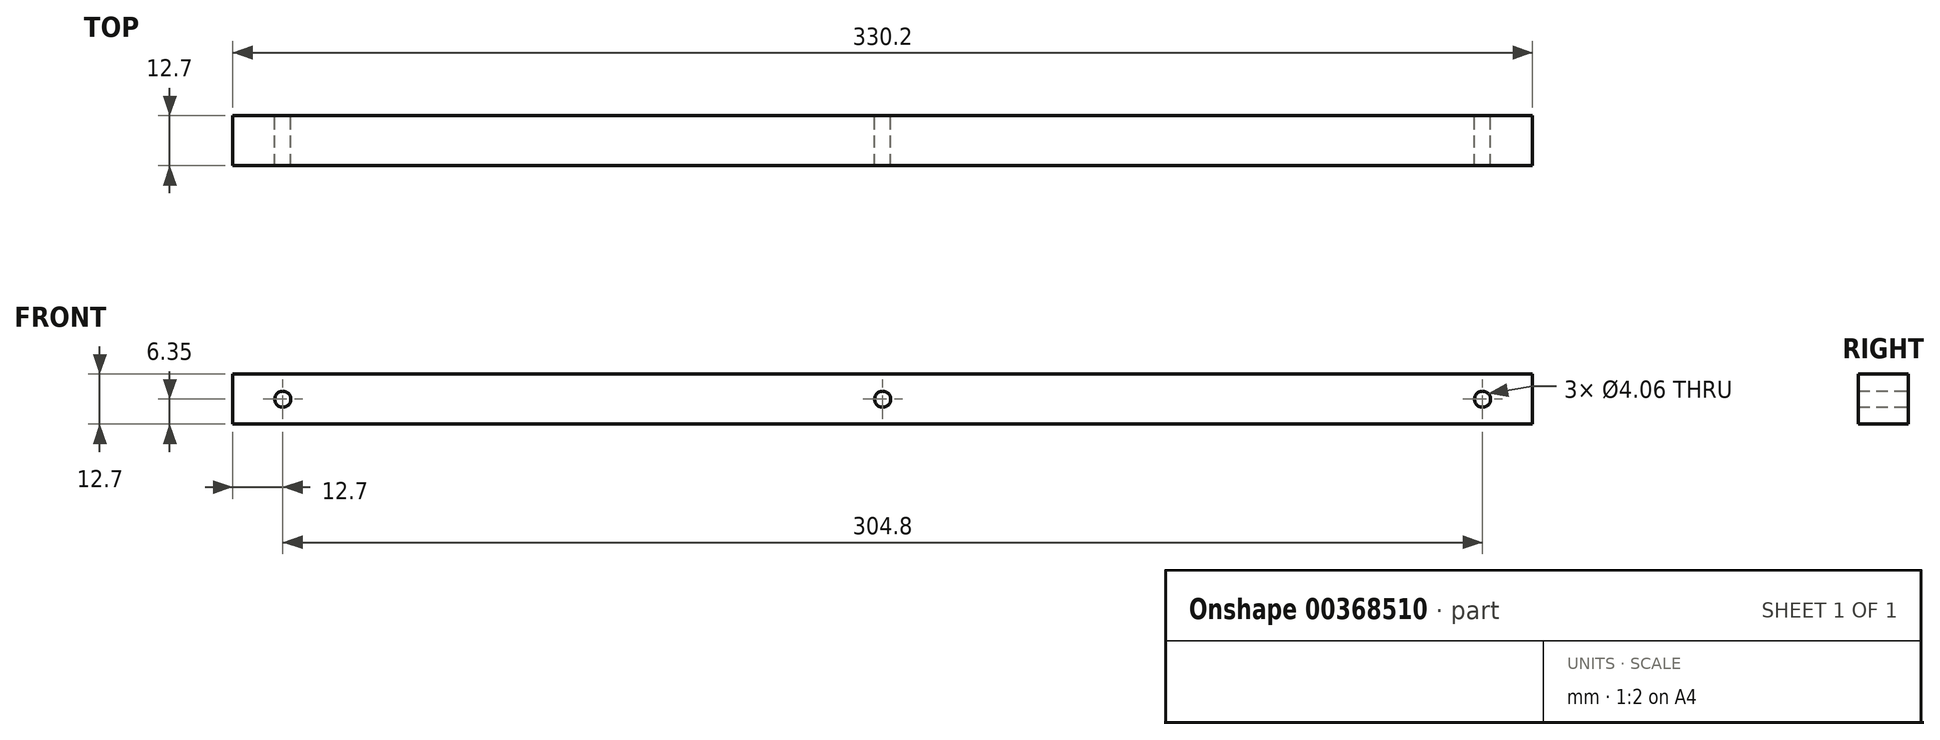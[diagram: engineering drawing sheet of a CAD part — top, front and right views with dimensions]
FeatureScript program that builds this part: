
annotation { "Feature Type Name" : "Feature", "Feature Type Description" : "" }
export const myFeature = defineFeature(function(context is Context, id is Id, definition is map)
    precondition{}
    {
        {
            var Q0;
            Q0=qCreatedBy(makeId("Front.planeOp"),FACE);
            var sketch = newSketch(context, id + "F0", { "sketchPlane" : qUnion([Q0])});
            skLineSegment(sketch, "E0.bottom", {"start": v(165.1, -6.35) * mm, "end": v(-165.1, -6.35) * mm});
            skLineSegment(sketch, "E0.top", {"start": v(165.1, 6.35) * mm, "end": v(-165.1, 6.35) * mm});
            skLineSegment(sketch, "E0.left", {"start": v(165.1, -6.35) * mm, "end": v(165.1, 6.35) * mm});
            skLineSegment(sketch, "E0.right", {"start": v(-165.1, -6.35) * mm, "end": v(-165.1, 6.35) * mm});
            skPoint(sketch, "E0.middle", {"position": v(0, 0) * mm});
            skCircle(sketch, "E1", {"center": v(0, 0) * mm, "radius": 2.03 * mm});
            skCircle(sketch, "E2", {"center": v(152.4, 0) * mm, "radius": 2.03 * mm});
            skPoint(sketch, "E2.centerSnap0", {"position": v(165.1, 0) * mm});
            skCircle(sketch, "E3", {"center": v(-152.4, 0) * mm, "radius": 2.03 * mm});
            skSolve(sketch);
        }
        {
            var Q0;
            Q0=makeQuery(id+"F0.imprint","IMPRINT",FACE,{"disambiguationData":[TD([[makeQuery(id+"F0.imprint","IMPRINT",EDGE,{"derivedFrom":sQuery(id+"F0.wireOp",EDGE,"E0.bottom")}),-1.0]])]});
            extrude(context, id + "F1", {"entities" : qUnion([Q0]), "depth" : 12.7 * mm});
        }
    });
